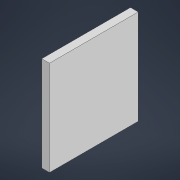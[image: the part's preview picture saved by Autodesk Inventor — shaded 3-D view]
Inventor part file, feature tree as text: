
AUTODESK INVENTOR PART (.ipt)
format: ipt  version: 2022 (Build 260153000, 153)  size: 86,016 bytes
history: native  units: mm
features: other x1, extrude x1, sketch x1
ambient origin geometry x8: Origin, YZ Plane, XZ Plane, XY Plane, X Axis, Y Axis, Z Axis, Center Point
bodies: Body1 (feature_tree)
feature tree (3):
  other  "Твердое тело1"
  extrude  "Выдавливание1"  Depth=270.0mm
  sketch  "Эскиз1"
